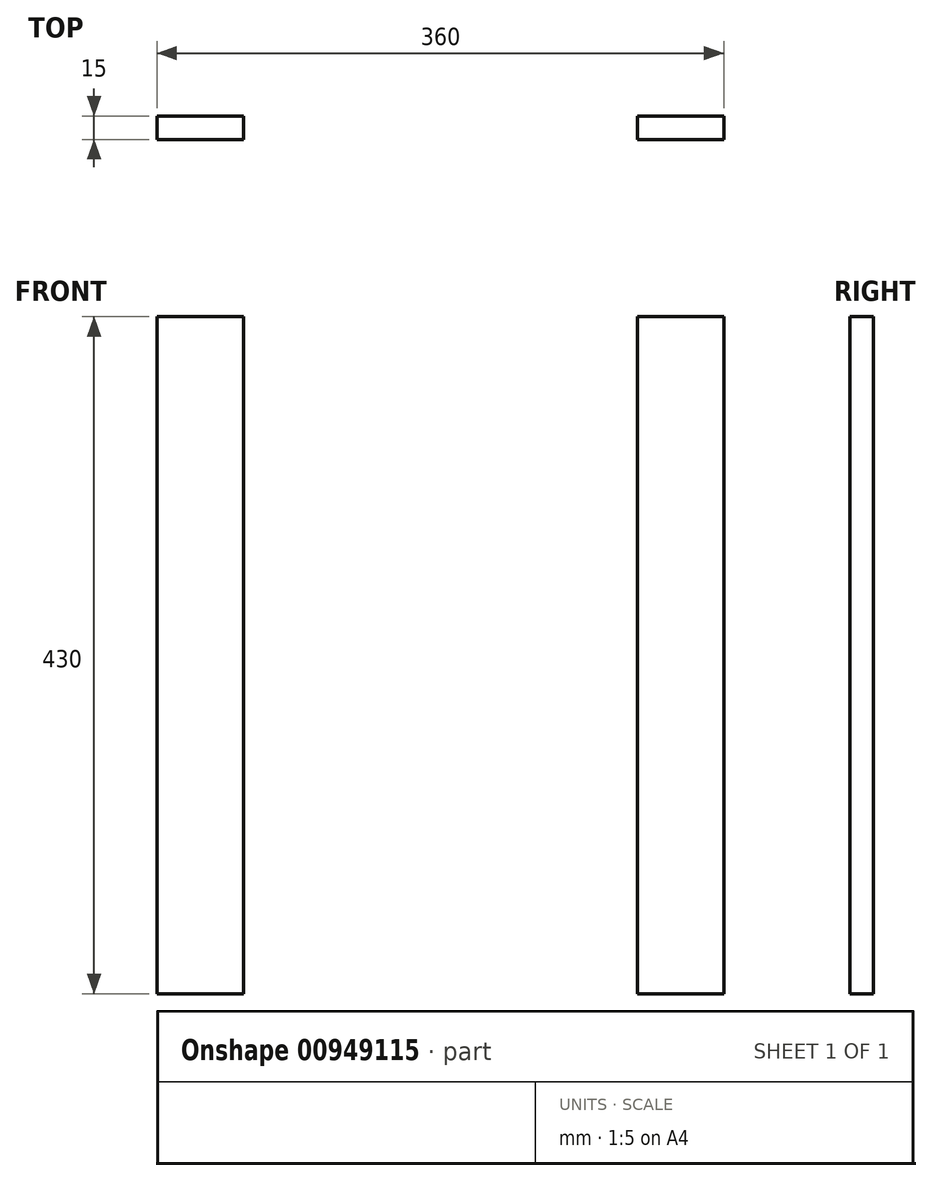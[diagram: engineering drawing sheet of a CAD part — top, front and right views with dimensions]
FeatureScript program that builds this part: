
annotation { "Feature Type Name" : "Feature", "Feature Type Description" : "" }
export const myFeature = defineFeature(function(context is Context, id is Id, definition is map)
    precondition{}
    {
        {
            assignVariable(context, id + "F0", {"name" : "Brettstaerke", "anyValue" : 15});
        }
        {
            var Q0;
            Q0=qCreatedBy(makeId("Front.planeOp"),FACE);
            var sketch = newSketch(context, id + "F1", { "sketchPlane" : qUnion([Q0])});
            skLineSegment(sketch, "E0.bottom", {"start": v(-180, 430) * mm, "end": v(-125, 430) * mm});
            skLineSegment(sketch, "E0.top", {"start": v(-180, 0) * mm, "end": v(-125, 0) * mm});
            skLineSegment(sketch, "E0.left", {"start": v(-180, 430) * mm, "end": v(-180, 0) * mm});
            skLineSegment(sketch, "E0.right", {"start": v(-125, 430) * mm, "end": v(-125, 0) * mm});
            skLineSegment(sketch, "E1.bottom", {"start": v(125, 430) * mm, "end": v(180, 430) * mm});
            skLineSegment(sketch, "E1.top", {"start": v(125, 0) * mm, "end": v(180, 0) * mm});
            skLineSegment(sketch, "E1.left", {"start": v(125, 430) * mm, "end": v(125, 0) * mm});
            skLineSegment(sketch, "E1.right", {"start": v(180, 430) * mm, "end": v(180, 0) * mm});
            skLineSegment(sketch, "E2", {"start": v(-125, 0) * mm, "end": v(125, 0) * mm, "construction": true});
            skSolve(sketch);
        }
        {
            var Q0;
            Q0 = qSketchRegion(id + "F1", true);
            extrude(context, id + "F2", {"entities" : qUnion([Q0]), "depth" : (getVariable(context, 'Brettstaerke')) * mm, "offsetDistance" : 25 * mm});
        }
    });
